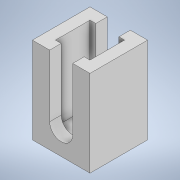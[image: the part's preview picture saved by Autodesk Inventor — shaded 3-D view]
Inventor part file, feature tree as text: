
AUTODESK INVENTOR PART (.ipt)
format: ipt  version: 2022 (Build 260153000, 153)  size: 111,104 bytes
history: native  units: in
note: dims shown in document units (in); Inventor stores cm internally (conversion verified against a paired STEP export)
features: extrude x2, sketch x2, shell x1
ambient origin geometry x8: Origin, YZ Plane, XZ Plane, XY Plane, X Axis, Y Axis, Z Axis, Center Point
bodies: Solid1 (feature_tree)
feature tree (5):
  extrude  "Extrusion1"  Depth=0.1969in
  shell  "Shell1"  Thickness=0.2953in
  extrude  "Extrusion3"  TaperAngle=0.0deg  [1 undecoded]
  sketch  "Sketch1"  dims[d0=0.1969in d1=0.1969in d2=0.2953in d3=0.0in]
  sketch  "Sketch3"  dims[d4=0.0394in d8=0.0in d9=0.0in]
note: 1 required parameter value undecoded (feature->parameter linkage not recoverable at this tier; creation-order binding heuristic only, values carry confidence <= 0.55)
